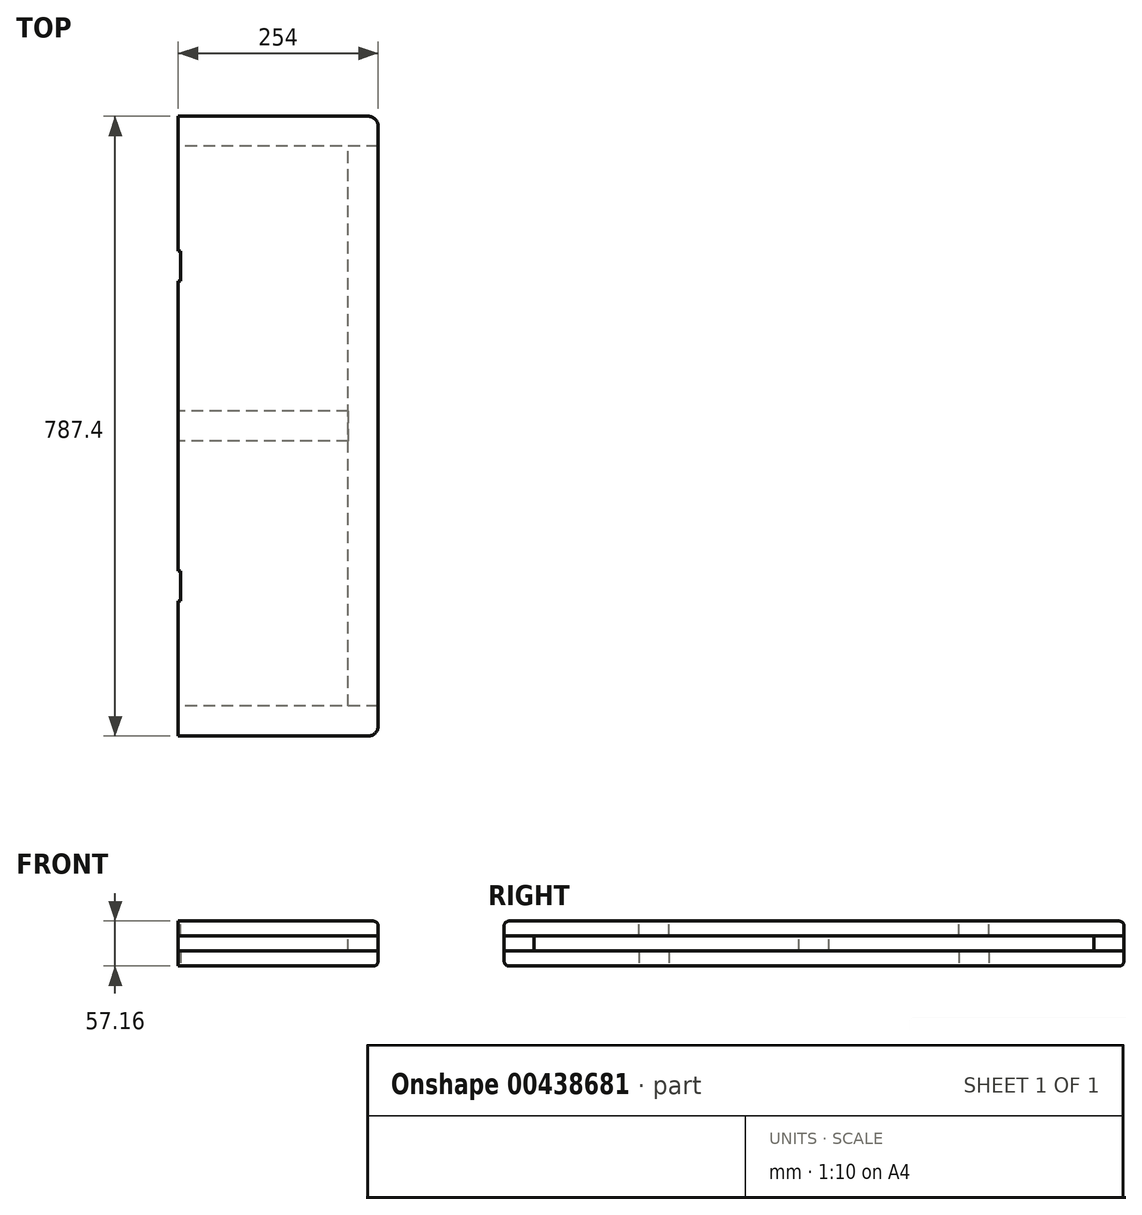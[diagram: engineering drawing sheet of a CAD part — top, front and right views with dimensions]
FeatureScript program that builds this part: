
annotation { "Feature Type Name" : "Feature", "Feature Type Description" : "" }
export const myFeature = defineFeature(function(context is Context, id is Id, definition is map)
    precondition{}
    {
        {
            var Q0;
            Q0=qCreatedBy(makeId("Right.planeOp"),FACE);
            var sketch = newSketch(context, id + "F0", { "sketchPlane" : qUnion([Q0])});
            skLineSegment(sketch, "E0.bottom", {"start": v(-393.7, -9.53) * mm, "end": v(-355.6, -9.53) * mm});
            skLineSegment(sketch, "E0.top", {"start": v(-393.7, 9.53) * mm, "end": v(-355.6, 9.53) * mm});
            skLineSegment(sketch, "E0.left", {"start": v(-393.7, -9.53) * mm, "end": v(-393.7, 9.53) * mm});
            skLineSegment(sketch, "E0.right", {"start": v(-355.6, -9.53) * mm, "end": v(-355.6, 9.53) * mm});
            skLineSegment(sketch, "E1.MirrorCS", {"start": v(393.7, -9.53) * mm, "end": v(355.6, -9.53) * mm});
            skLineSegment(sketch, "E2.MirrorCS", {"start": v(393.7, 9.53) * mm, "end": v(355.6, 9.53) * mm});
            skLineSegment(sketch, "E3.MirrorCS", {"start": v(393.7, -9.53) * mm, "end": v(393.7, 9.53) * mm});
            skLineSegment(sketch, "E4.MirrorCS", {"start": v(355.6, -9.53) * mm, "end": v(355.6, 9.53) * mm});
            skLineSegment(sketch, "E5.bottom", {"start": v(-19.05, 9.53) * mm, "end": v(19.05, 9.53) * mm});
            skLineSegment(sketch, "E5.top", {"start": v(-19.05, -9.53) * mm, "end": v(19.05, -9.53) * mm});
            skLineSegment(sketch, "E5.left", {"start": v(-19.05, 9.52) * mm, "end": v(-19.05, -9.53) * mm});
            skLineSegment(sketch, "E5.right", {"start": v(19.05, 9.52) * mm, "end": v(19.05, -9.53) * mm});
            skSolve(sketch);
        }
        {
            var Q0;
            Q0=makeQuery(id+"F0.imprint","IMPRINT",FACE,{"disambiguationData":[TD([[makeQuery(id+"F0.imprint","IMPRINT",EDGE,{"derivedFrom":sQuery(id+"F0.wireOp",EDGE,"E0.bottom")}),1.0]])]});
            var Q1;
            Q1=makeQuery(id+"F0.imprint","IMPRINT",FACE,{"disambiguationData":[TD([[makeQuery(id+"F0.imprint","IMPRINT",EDGE,{"derivedFrom":sQuery(id+"F0.wireOp",EDGE,"E1.MirrorCS")}),-1.0]])]});
            extrude(context, id + "F1", {"entities" : qUnion([Q0, Q1]), "depth" : 254 * mm, "offsetDistance" : 25.4 * mm});
        }
        {
            var Q0;
            Q0=qCreatedBy(makeId("Front.planeOp"),FACE);
            var sketch = newSketch(context, id + "F2", { "sketchPlane" : qUnion([Q0])});
            skLineSegment(sketch, "E6.0", {"start": v(254, -9.53) * mm, "end": v(254, 9.53) * mm});
            skLineSegment(sketch, "E7.bottom", {"start": v(254, -9.53) * mm, "end": v(215.9, -9.53) * mm});
            skLineSegment(sketch, "E7.top", {"start": v(254, 9.53) * mm, "end": v(215.9, 9.52) * mm});
            skLineSegment(sketch, "E7.left", {"start": v(254, -9.52) * mm, "end": v(254, 9.53) * mm});
            skLineSegment(sketch, "E7.right", {"start": v(215.9, -9.53) * mm, "end": v(215.9, 9.52) * mm});
            skSolve(sketch);
        }
        {
            var Q0;
            Q0 = qSketchRegion(id + "F2", true);
            extrude(context, id + "F3", {"entities" : qUnion([Q0]), "endBound" : BoundingType.SYMMETRIC, "depth" : 711.2 * mm, "offsetDistance" : 25.4 * mm});
        }
        {
            var Q0;
            Q0=makeQuery(id+"F0.imprint","IMPRINT",FACE,{"disambiguationData":[TD([[makeQuery(id+"F0.imprint","IMPRINT",EDGE,{"derivedFrom":sQuery(id+"F0.wireOp",EDGE,"E5.bottom")}),-1.0]])]});
            var Q1;
            Q1=makeQuery(id+"F3.opExtrude","SWEPT_FACE",FACE,{"disambiguationData":[OSD([sQuery(id+"F2.wireOp",EDGE,"E7.right")])]});
            extrude(context, id + "F4", {"entities" : qUnion([Q0]), "endBound" : BoundingType.UP_TO_SURFACE, "depth" : 25.4 * mm, "endBoundEntityFace" : qUnion([Q1]), "offsetDistance" : 25.4 * mm});
        }
        {
            var Q0;
            Q0=makeQuery(id+"F1.opExtrude","CAP_EDGE",EDGE,{"disambiguationData":[OSD([sQuery(id+"F0.wireOp",EDGE,"E0.left")])],"isStart":false});
            var Q1;
            Q1=makeQuery(id+"F1.opExtrude","CAP_EDGE",EDGE,{"disambiguationData":[OSD([sQuery(id+"F0.wireOp",EDGE,"E3.MirrorCS")])],"isStart":false});
            fillet(context, id + "F5", {"entities" : qUnion([Q0, Q1]), "radius" : 12.7 * mm, "tangentPropagation" : true, "allowEdgeOverflow" : false});
        }
        {
            var Q0;
            Q0=makeQuery(id+"F3.opExtrude","SWEPT_FACE",FACE,{"disambiguationData":[OSD([sQuery(id+"F2.wireOp",EDGE,"E7.top")])]});
            var sketch = newSketch(context, id + "F6", { "sketchPlane" : qUnion([Q0])});
            skLineSegment(sketch, "E8.0", {"start": v(241.3, -393.7) * mm, "end": v(0, -393.7) * mm});
            skArc(sketch, "E9.0", {"start": v(241.3, -393.7) * mm, "mid": v(250.28, -389.98) * mm, "end": v(254, -381) * mm});
            skArc(sketch, "E10.0", {"start": v(254, 381) * mm, "mid": v(250.28, 389.98) * mm, "end": v(241.3, 393.7) * mm});
            skLineSegment(sketch, "E11.0", {"start": v(241.3, 393.7) * mm, "end": v(0, 393.7) * mm});
            skLineSegment(sketch, "E12", {"start": v(254, -381) * mm, "end": v(254, 381) * mm});
            skLineSegment(sketch, "E13", {"start": v(0, -393.7) * mm, "end": v(0, 393.7) * mm});
            skSolve(sketch);
        }
        {
            var Q0;
            {var subQ1=sQuery(id+"F2.wireOp",EDGE,"E7.top");var subQ2=makeQuery(id+"F3.opExtrude","CAP_EDGE",EDGE,{"disambiguationData":[OSD([subQ1])],"isStart":true});Q0=makeQuery(id+"F6.imprint","IMPRINT",FACE,{"disambiguationData":[TD([[makeQuery(id+"F6.imprint","IMPRINT",EDGE,{"derivedFrom":subQ2}),1.0]])]});}
            var Q1;
            Q1=makeQuery(id+"F6.imprint","IMPRINT",FACE,{"disambiguationData":[TD([[makeQuery(id+"F6.imprint","IMPRINT",EDGE,{"derivedFrom":sQuery(id+"F6.wireOp",EDGE,"E8.0")}),-1.0]])]});
            extrude(context, id + "F7", {"entities" : qUnion([Q0, Q1]), "depth" : 19.05 * mm, "offsetDistance" : 25.4 * mm});
        }
        {
            var Q0;
            Q0=makeQuery(id+"F7.opExtrude","CAP_FACE",FACE,{"disambiguationData":[OSD([sQuery(id+"F6.wireOp",EDGE,"E8.0"),sQuery(id+"F6.wireOp",EDGE,"E9.0"),sQuery(id+"F6.wireOp",EDGE,"E10.0"),sQuery(id+"F6.wireOp",EDGE,"E11.0"),sQuery(id+"F6.wireOp",EDGE,"E12"),sQuery(id+"F6.wireOp",EDGE,"E13")])],"isStart":false});
            var sketch = newSketch(context, id + "F8", { "sketchPlane" : qUnion([Q0])});
            skLineSegment(sketch, "E14.bottom", {"start": v(0, -222.25) * mm, "end": v(3.17, -222.25) * mm});
            skLineSegment(sketch, "E14.top", {"start": v(0, -184.15) * mm, "end": v(3.17, -184.15) * mm});
            skLineSegment(sketch, "E14.left", {"start": v(0, -222.25) * mm, "end": v(0, -184.15) * mm});
            skLineSegment(sketch, "E14.right", {"start": v(3.17, -222.25) * mm, "end": v(3.17, -184.15) * mm});
            skLineSegment(sketch, "E15.MirrorCS", {"start": v(0, 184.15) * mm, "end": v(3.17, 184.15) * mm});
            skLineSegment(sketch, "E16.MirrorCS", {"start": v(0, 222.25) * mm, "end": v(3.17, 222.25) * mm});
            skLineSegment(sketch, "E17.MirrorCS", {"start": v(0, 222.25) * mm, "end": v(0, 184.15) * mm});
            skLineSegment(sketch, "E18.MirrorCS", {"start": v(3.17, 222.25) * mm, "end": v(3.17, 184.15) * mm});
            skSolve(sketch);
        }
        {
            var Q0;
            Q0=makeQuery(id+"F7.opExtrude","CAP_EDGE",EDGE,{"disambiguationData":[OSD([sQuery(id+"F6.wireOp",EDGE,"E8.0")])],"isStart":false});
            fillet(context, id + "F9", {"entities" : qUnion([Q0]), "radius" : 6.35 * mm, "tangentPropagation" : true, "allowEdgeOverflow" : false});
        }
        {
            var Q0;
            Q0=makeQuery(id+"F7.opExtrude","SWEPT_BODY",BODY,{"disambiguationData":[OSD([sQuery(id+"F6.wireOp",EDGE,"E8.0"),sQuery(id+"F6.wireOp",EDGE,"E9.0"),sQuery(id+"F6.wireOp",EDGE,"E10.0"),sQuery(id+"F6.wireOp",EDGE,"E11.0"),sQuery(id+"F6.wireOp",EDGE,"E12"),sQuery(id+"F6.wireOp",EDGE,"E13")])]});
            var Q1;
            Q1=qCreatedBy(makeId("Top.planeOp"),FACE);
            mirror(context, id + "F10", {"entities" : qUnion([Q0]), "mirrorPlane" : qUnion([Q1])});
        }
        {
            var Q0;
            Q0=makeQuery(id+"F8.imprint","IMPRINT",FACE,{"disambiguationData":[TD([[makeQuery(id+"F8.imprint","IMPRINT",EDGE,{"derivedFrom":sQuery(id+"F8.wireOp",EDGE,"E14.bottom")}),1.0]])]});
            var Q1;
            Q1=makeQuery(id+"F8.imprint","IMPRINT",FACE,{"disambiguationData":[TD([[makeQuery(id+"F8.imprint","IMPRINT",EDGE,{"derivedFrom":sQuery(id+"F8.wireOp",EDGE,"E16.MirrorCS")}),-1.0]])]});
            extrude(context, id + "F11", {"entities" : qUnion([Q0, Q1]), "operationType" : NewBodyOperationType.REMOVE, "endBound" : BoundingType.THROUGH_ALL, "oppositeDirection" : true, "depth" : 25.4 * mm, "offsetDistance" : 25.4 * mm});
        }
        {
            var Q0;
            Q0=makeQuery(id+"F10.opPattern","COPY",BODY,{"derivedFrom":makeQuery(id+"F7.opExtrude","SWEPT_BODY",BODY,{"disambiguationData":[OSD([sQuery(id+"F6.wireOp",EDGE,"E8.0"),sQuery(id+"F6.wireOp",EDGE,"E9.0"),sQuery(id+"F6.wireOp",EDGE,"E10.0"),sQuery(id+"F6.wireOp",EDGE,"E11.0"),sQuery(id+"F6.wireOp",EDGE,"E12"),sQuery(id+"F6.wireOp",EDGE,"E13")])]}),"instanceName":"1"});
            deleteBodies(context, id + "F12", {"entities" : qUnion([Q0])});
        }
        {
            var Q0;
            Q0=makeQuery(id+"F7.opExtrude","SWEPT_BODY",BODY,{"disambiguationData":[OSD([sQuery(id+"F6.wireOp",EDGE,"E8.0"),sQuery(id+"F6.wireOp",EDGE,"E9.0"),sQuery(id+"F6.wireOp",EDGE,"E10.0"),sQuery(id+"F6.wireOp",EDGE,"E11.0"),sQuery(id+"F6.wireOp",EDGE,"E12"),sQuery(id+"F6.wireOp",EDGE,"E13")])]});
            var Q1;
            Q1=qCreatedBy(makeId("Top.planeOp"),FACE);
            mirror(context, id + "F13", {"entities" : qUnion([Q0]), "mirrorPlane" : qUnion([Q1])});
        }
    });
